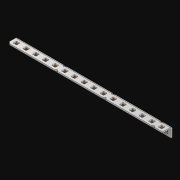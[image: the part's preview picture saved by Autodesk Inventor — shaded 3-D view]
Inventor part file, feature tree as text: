
AUTODESK INVENTOR PART (.ipt)
format: ipt  version: 2021 (Build 250183000, 183)  size: 683,520 bytes
history: native  units: in
note: dims shown in document units (in); Inventor stores cm internally (conversion verified against a paired STEP export)
features: extrude x33, other x32, sketch x3, pattern_linear x1, sheet_metal_op x1
ambient origin geometry x8: Origin, YZ Plane, XZ Plane, XY Plane, X Axis, Y Axis, Z Axis, Center Point
bodies: Solid1 (feature_tree)
feature tree (70):
  pattern_linear  "Rectangular Pattern1"  Spacing1=0.063in  [1 undecoded]
  extrude  "Extrusion1"  Depth=0.5in
  sketch  "Sketch1"  dims[d0=0.182in]
  other  "Srf1"
  sketch  "Sketch2"  dims[d1=0.063in d2=0.0in]
  other  "Srf2"
  other  "Srf3"
  other  "Srf5"
  other  "Srf7"
  other  "Srf9"
  other  "Srf11"
  other  "Srf13"
  other  "Srf15"
  other  "Srf17"
  other  "Srf19"
  other  "Srf21"
  other  "Srf23"
  other  "Srf25"
  other  "Srf27"
  other  "Srf29"
  other  "Srf31"
  other  "Srf4"
  other  "Srf6"
  other  "Srf8"
  other  "Srf10"
  other  "Srf12"
  other  "Srf14"
  other  "Srf16"
  other  "Srf18"
  other  "Srf20"
  other  "Srf22"
  other  "Srf24"
  other  "Srf26"
  other  "Srf28"
  other  "Srf30"
  other  "Srf32"
  sketch  "Sketch3"  dims[d3=0.182in d4=0.063in d5=0.0in d8=0.5in d9=9.5in d10=0.0in]
  sheet_metal_op  "Fold1"
  extrude  "ExtrusionSrf1"  Depth=0.5in TaperAngle=0.0deg
  extrude  "ExtrusionSrf2"  [1 undecoded]
  extrude  "ExtrusionSrf3"  [1 undecoded]
  extrude  "ExtrusionSrf4"  [1 undecoded]
  extrude  "ExtrusionSrf5"  [1 undecoded]
  extrude  "ExtrusionSrf6"  [1 undecoded]
  extrude  "ExtrusionSrf7"  [1 undecoded]
  extrude  "ExtrusionSrf8"  [1 undecoded]
  extrude  "ExtrusionSrf9"  [1 undecoded]
  extrude  "ExtrusionSrf10"  [1 undecoded]
  extrude  "ExtrusionSrf11"  [1 undecoded]
  extrude  "ExtrusionSrf12"  [1 undecoded]
  extrude  "ExtrusionSrf13"  [1 undecoded]
  extrude  "ExtrusionSrf14"  [1 undecoded]
  extrude  "ExtrusionSrf15"  [1 undecoded]
  extrude  "ExtrusionSrf16"  [1 undecoded]
  extrude  "ExtrusionSrf17"  [1 undecoded]
  extrude  "ExtrusionSrf37"  [1 undecoded]
  extrude  "ExtrusionSrf38"  [1 undecoded]
  extrude  "ExtrusionSrf39"  [1 undecoded]
  extrude  "ExtrusionSrf40"  [1 undecoded]
  extrude  "ExtrusionSrf41"  [1 undecoded]
  extrude  "ExtrusionSrf42"  [1 undecoded]
  extrude  "ExtrusionSrf43"  [1 undecoded]
  extrude  "ExtrusionSrf44"  [1 undecoded]
  extrude  "ExtrusionSrf45"  [1 undecoded]
  extrude  "ExtrusionSrf46"  [1 undecoded]
  extrude  "ExtrusionSrf47"  [1 undecoded]
  extrude  "ExtrusionSrf48"  [1 undecoded]
  extrude  "ExtrusionSrf49"  [1 undecoded]
  extrude  "ExtrusionSrf50"  [1 undecoded]
  extrude  "ExtrusionSrf51"  [1 undecoded]
note: 32 required parameter values undecoded (feature->parameter linkage not recoverable at this tier; creation-order binding heuristic only, values carry confidence <= 0.55)
